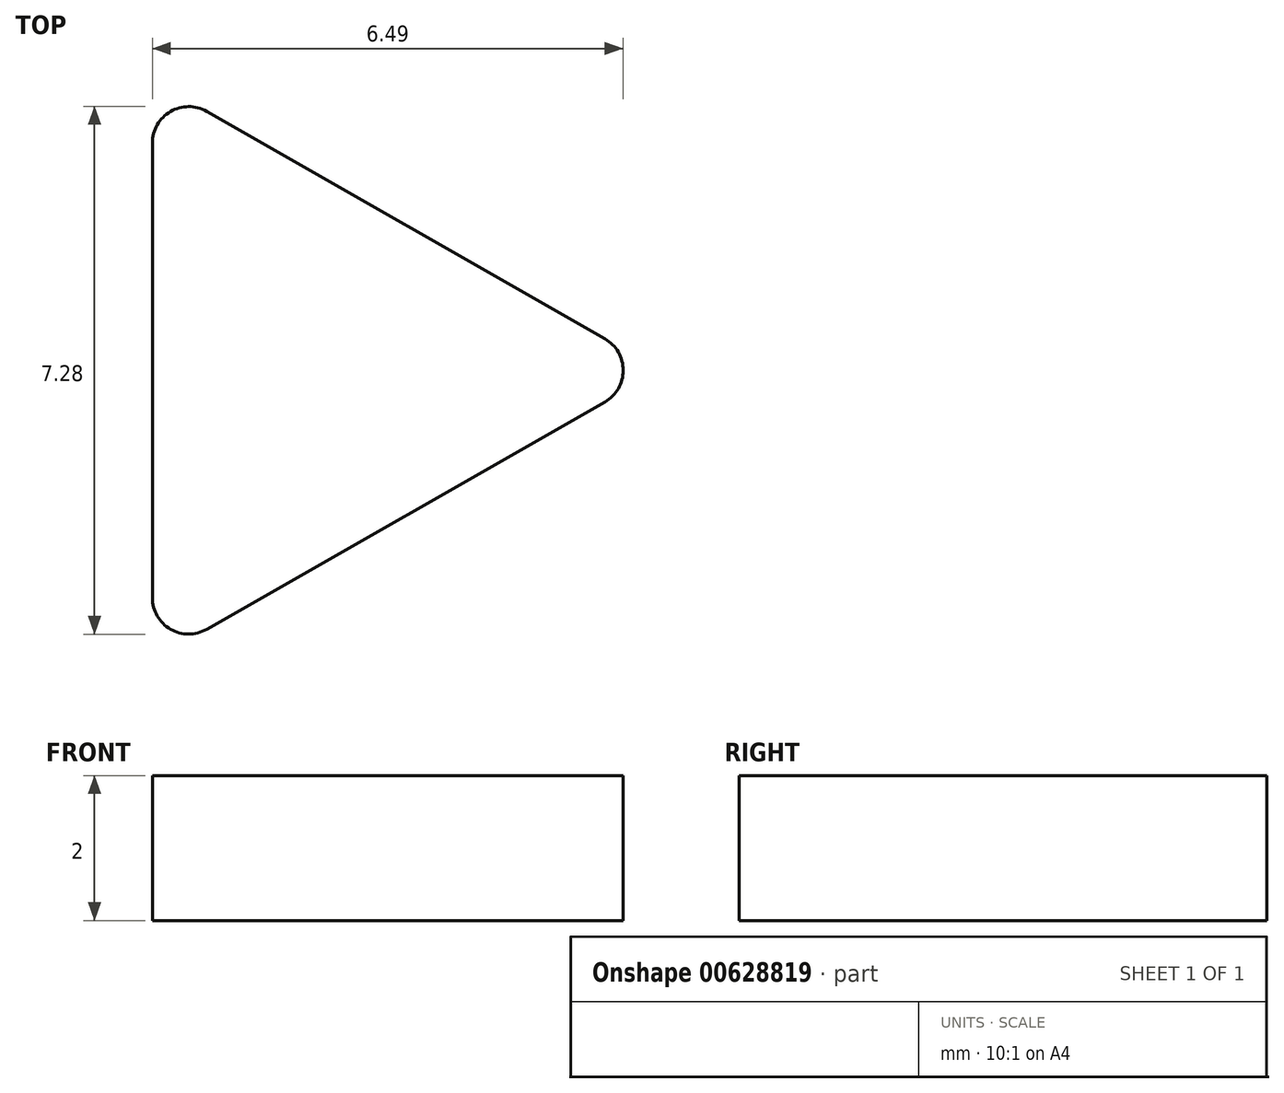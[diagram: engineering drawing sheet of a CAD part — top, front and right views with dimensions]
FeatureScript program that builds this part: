
annotation { "Feature Type Name" : "Feature", "Feature Type Description" : "" }
export const myFeature = defineFeature(function(context is Context, id is Id, definition is map)
    precondition{}
    {
        {
            var Q0;
            Q0=qCreatedBy(makeId("Top.planeOp"),FACE);
            var sketch = newSketch(context, id + "F0", { "sketchPlane" : qUnion([Q0])});
            skLineSegment(sketch, "E0", {"start": v(2.74, 0.43) * mm, "end": v(-2.75, 3.57) * mm});
            skLineSegment(sketch, "E1", {"start": v(-3.5, 3.14) * mm, "end": v(-3.5, -3.14) * mm});
            skLineSegment(sketch, "E2", {"start": v(-2.75, -3.57) * mm, "end": v(2.74, -0.43) * mm});
            skPoint(sketch, "E3.visualSharp", {"position": v(-3.5, 4) * mm});
            skArc(sketch, "E3.filletArc", {"start": v(-2.75, 3.57) * mm, "mid": v(-3.25, 3.57) * mm, "end": v(-3.5, 3.14) * mm});
            skPoint(sketch, "E4.visualSharp", {"position": v(3.5, 0) * mm});
            skArc(sketch, "E4.filletArc", {"start": v(2.74, -0.43) * mm, "mid": v(3, 0) * mm, "end": v(2.74, 0.43) * mm});
            skPoint(sketch, "E5.visualSharp", {"position": v(-3.5, -4) * mm});
            skArc(sketch, "E5.filletArc", {"start": v(-3.5, -3.14) * mm, "mid": v(-3.25, -3.57) * mm, "end": v(-2.75, -3.57) * mm});
            skSolve(sketch);
        }
        {
            var Q0;
            Q0 = qSketchRegion(id + "F0", true);
            extrude(context, id + "F1", {"entities" : qUnion([Q0]), "depth" : 2 * mm, "offsetDistance" : 25 * mm, "symmetric" : true});
        }
    });
